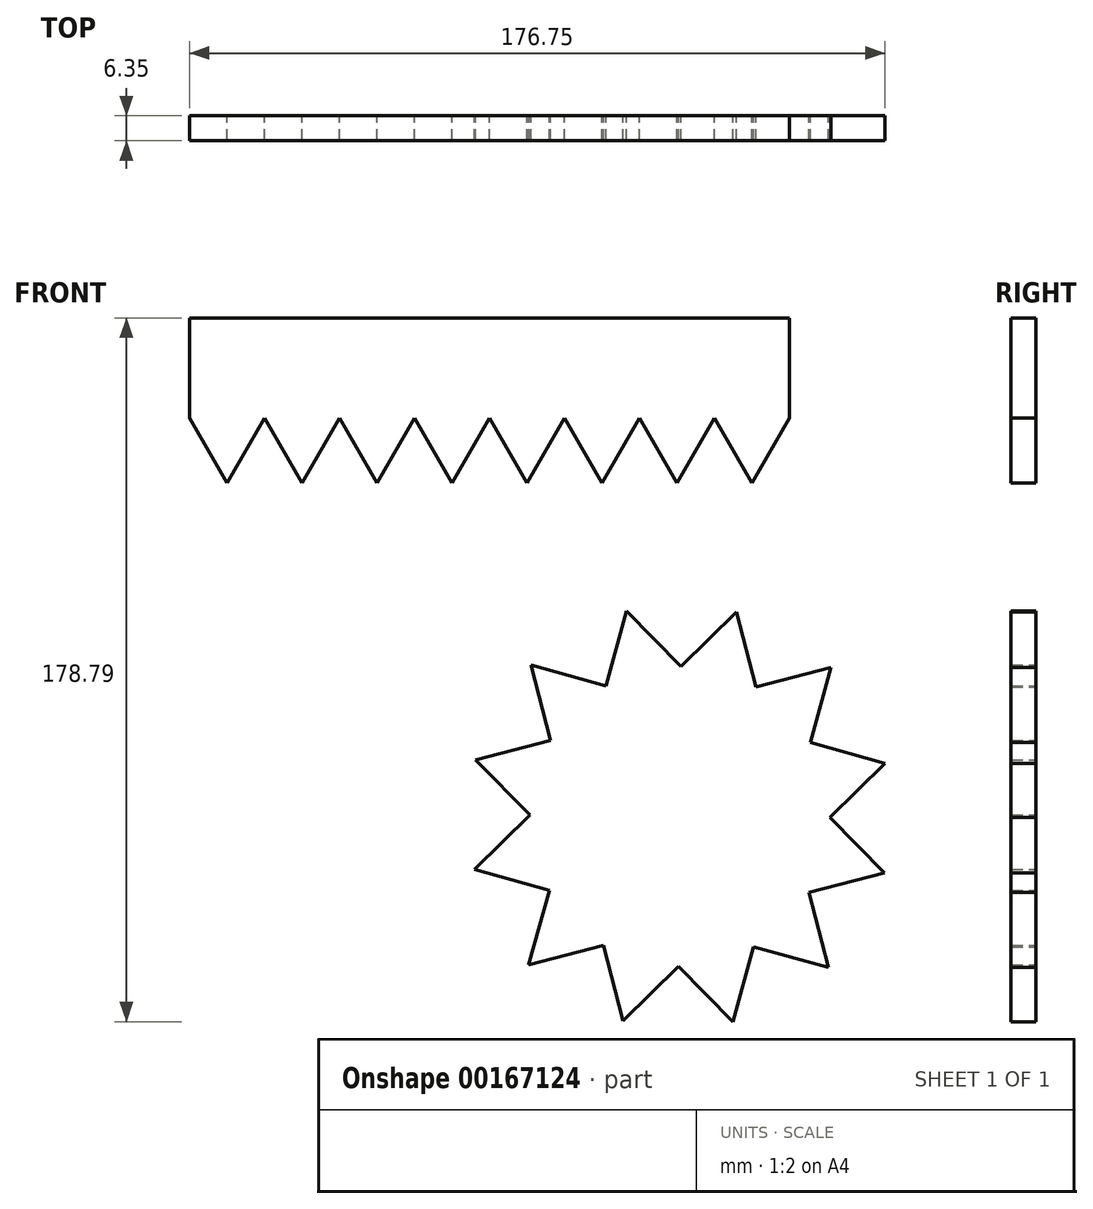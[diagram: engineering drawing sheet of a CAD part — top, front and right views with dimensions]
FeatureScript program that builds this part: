
annotation { "Feature Type Name" : "Feature", "Feature Type Description" : "" }
export const myFeature = defineFeature(function(context is Context, id is Id, definition is map)
    precondition{}
    {
        {
            var Q0;
            Q0=qCreatedBy(makeId("Front.planeOp"),FACE);
            var sketch = newSketch(context, id + "F0", { "sketchPlane" : qUnion([Q0])});
            skCircle(sketch, "E0", {"center": v(0, -57.84) * mm, "radius": 38.1 * mm});
            skCircle(sketch, "E1.cCircle", {"center": v(0, -57.84) * mm, "radius": 38.1 * mm, "construction": true});
            skLineSegment(sketch, "E1.0", {"start": v(33.16, -39.07) * mm, "end": v(38.1, -58.17) * mm});
            skLineSegment(sketch, "E1.1", {"start": v(38.1, -58.17) * mm, "end": v(32.83, -77.17) * mm});
            skLineSegment(sketch, "E1.2", {"start": v(32.83, -77.17) * mm, "end": v(18.77, -91) * mm});
            skLineSegment(sketch, "E1.3", {"start": v(18.77, -91) * mm, "end": v(-0.33, -95.94) * mm});
            skLineSegment(sketch, "E1.4", {"start": v(-0.33, -95.94) * mm, "end": v(-19.33, -90.67) * mm});
            skLineSegment(sketch, "E1.5", {"start": v(-19.33, -90.67) * mm, "end": v(-33.16, -76.6) * mm});
            skLineSegment(sketch, "E1.6", {"start": v(-33.16, -76.6) * mm, "end": v(-38.1, -57.51) * mm});
            skLineSegment(sketch, "E1.7", {"start": v(-38.1, -57.51) * mm, "end": v(-32.83, -38.5) * mm});
            skLineSegment(sketch, "E1.8", {"start": v(-32.83, -38.5) * mm, "end": v(-18.77, -24.68) * mm});
            skLineSegment(sketch, "E1.9", {"start": v(-18.77, -24.68) * mm, "end": v(0.33, -19.74) * mm});
            skLineSegment(sketch, "E1.10", {"start": v(0.33, -19.74) * mm, "end": v(19.33, -25) * mm});
            skLineSegment(sketch, "E1.11", {"start": v(19.33, -25) * mm, "end": v(33.16, -39.07) * mm});
            skLineSegment(sketch, "E2", {"start": v(-32.83, -38.5) * mm, "end": v(-37.77, -19.42) * mm});
            skLineSegment(sketch, "E3", {"start": v(-37.77, -19.42) * mm, "end": v(-18.77, -24.68) * mm});
            skLineSegment(sketch, "E4.1.0", {"start": v(-38.1, -57.51) * mm, "end": v(-51.92, -43.45) * mm});
            skLineSegment(sketch, "E4.1.1", {"start": v(-51.92, -43.45) * mm, "end": v(-32.83, -38.5) * mm});
            skLineSegment(sketch, "E4.2.0", {"start": v(-33.16, -76.6) * mm, "end": v(-52.16, -71.34) * mm});
            skLineSegment(sketch, "E4.2.1", {"start": v(-52.16, -71.34) * mm, "end": v(-38.1, -57.51) * mm});
            skLineSegment(sketch, "E4.3.0", {"start": v(-19.33, -90.67) * mm, "end": v(-38.43, -95.61) * mm});
            skLineSegment(sketch, "E4.3.1", {"start": v(-38.43, -95.61) * mm, "end": v(-33.16, -76.6) * mm});
            skLineSegment(sketch, "E4.4.0", {"start": v(-0.33, -95.94) * mm, "end": v(-14.4, -109.76) * mm});
            skLineSegment(sketch, "E4.4.1", {"start": v(-14.4, -109.76) * mm, "end": v(-19.33, -90.67) * mm});
            skLineSegment(sketch, "E4.5.0", {"start": v(18.77, -91) * mm, "end": v(13.5, -110) * mm});
            skLineSegment(sketch, "E4.5.1", {"start": v(13.5, -110) * mm, "end": v(-0.33, -95.94) * mm});
            skLineSegment(sketch, "E4.6.0", {"start": v(32.83, -77.17) * mm, "end": v(37.77, -96.27) * mm});
            skLineSegment(sketch, "E4.6.1", {"start": v(37.77, -96.27) * mm, "end": v(18.77, -91) * mm});
            skLineSegment(sketch, "E4.7.0", {"start": v(38.1, -58.17) * mm, "end": v(51.92, -72.23) * mm});
            skLineSegment(sketch, "E4.7.1", {"start": v(51.92, -72.23) * mm, "end": v(32.83, -77.17) * mm});
            skLineSegment(sketch, "E4.8.0", {"start": v(33.16, -39.07) * mm, "end": v(52.16, -44.34) * mm});
            skLineSegment(sketch, "E4.8.1", {"start": v(52.16, -44.34) * mm, "end": v(38.1, -58.17) * mm});
            skLineSegment(sketch, "E4.9.0", {"start": v(19.33, -25) * mm, "end": v(38.43, -20.07) * mm});
            skLineSegment(sketch, "E4.9.1", {"start": v(38.43, -20.07) * mm, "end": v(33.16, -39.07) * mm});
            skLineSegment(sketch, "E4.10.0", {"start": v(0.33, -19.74) * mm, "end": v(14.4, -5.92) * mm});
            skLineSegment(sketch, "E4.10.1", {"start": v(14.4, -5.92) * mm, "end": v(19.33, -25) * mm});
            skLineSegment(sketch, "E4.11.0", {"start": v(-18.77, -24.68) * mm, "end": v(-13.5, -5.68) * mm});
            skLineSegment(sketch, "E4.11.1", {"start": v(-13.5, -5.68) * mm, "end": v(0.33, -19.74) * mm});
            skSolve(sketch);
        }
        {
            var Q0;
            Q0 = qSketchRegion(id + "F0", true);
            extrude(context, id + "F1", {"entities" : qUnion([Q0]), "depth" : 6.35 * mm});
        }
        {
            var Q0;
            Q0=qCreatedBy(makeId("Front.planeOp"),FACE);
            var sketch = newSketch(context, id + "F2", { "sketchPlane" : qUnion([Q0])});
            skLineSegment(sketch, "E5.bottom", {"start": v(-124.6, 68.79) * mm, "end": v(27.8, 68.79) * mm});
            skLineSegment(sketch, "E5.top", {"start": v(-124.6, 43.39) * mm, "end": v(27.8, 43.39) * mm});
            skLineSegment(sketch, "E5.left", {"start": v(-124.6, 68.79) * mm, "end": v(-124.6, 43.39) * mm});
            skLineSegment(sketch, "E5.right", {"start": v(27.8, 68.79) * mm, "end": v(27.8, 43.39) * mm});
            skLineSegment(sketch, "E6", {"start": v(-124.6, 43.39) * mm, "end": v(-115.07, 26.89) * mm});
            skLineSegment(sketch, "E7", {"start": v(-115.07, 26.89) * mm, "end": v(-105.54, 43.39) * mm});
            skLineSegment(sketch, "E8.1.0.0", {"start": v(-105.54, 43.39) * mm, "end": v(-96.02, 26.89) * mm});
            skLineSegment(sketch, "E8.1.0.1", {"start": v(-105.54, 43.39) * mm, "end": v(46.86, 43.39) * mm});
            skLineSegment(sketch, "E8.1.0.2", {"start": v(-96.02, 26.89) * mm, "end": v(-86.5, 43.39) * mm});
            skLineSegment(sketch, "E8.2.0.0", {"start": v(-86.5, 43.39) * mm, "end": v(-76.97, 26.89) * mm});
            skLineSegment(sketch, "E8.2.0.1", {"start": v(-86.5, 43.39) * mm, "end": v(65.9, 43.39) * mm});
            skLineSegment(sketch, "E8.2.0.2", {"start": v(-76.97, 26.89) * mm, "end": v(-67.44, 43.39) * mm});
            skLineSegment(sketch, "E8.3.0.0", {"start": v(-67.44, 43.39) * mm, "end": v(-57.92, 26.89) * mm});
            skLineSegment(sketch, "E8.3.0.1", {"start": v(-67.44, 43.39) * mm, "end": v(84.96, 43.39) * mm});
            skLineSegment(sketch, "E8.3.0.2", {"start": v(-57.92, 26.89) * mm, "end": v(-48.4, 43.39) * mm});
            skLineSegment(sketch, "E8.4.0.0", {"start": v(-48.4, 43.39) * mm, "end": v(-38.87, 26.89) * mm});
            skLineSegment(sketch, "E8.4.0.1", {"start": v(-48.4, 43.39) * mm, "end": v(104, 43.39) * mm});
            skLineSegment(sketch, "E8.4.0.2", {"start": v(-38.87, 26.89) * mm, "end": v(-29.34, 43.39) * mm});
            skLineSegment(sketch, "E8.5.0.0", {"start": v(-29.34, 43.39) * mm, "end": v(-19.82, 26.89) * mm});
            skLineSegment(sketch, "E8.5.0.1", {"start": v(-29.34, 43.39) * mm, "end": v(123.06, 43.39) * mm});
            skLineSegment(sketch, "E8.5.0.2", {"start": v(-19.82, 26.89) * mm, "end": v(-10.3, 43.39) * mm});
            skLineSegment(sketch, "E8.6.0.0", {"start": v(-10.3, 43.39) * mm, "end": v(-0.77, 26.89) * mm});
            skLineSegment(sketch, "E8.6.0.1", {"start": v(-10.3, 43.39) * mm, "end": v(142.1, 43.39) * mm});
            skLineSegment(sketch, "E8.6.0.2", {"start": v(-0.77, 26.89) * mm, "end": v(8.76, 43.39) * mm});
            skLineSegment(sketch, "E8.7.0.0", {"start": v(8.76, 43.39) * mm, "end": v(18.28, 26.89) * mm});
            skLineSegment(sketch, "E8.7.0.1", {"start": v(8.76, 43.39) * mm, "end": v(161.16, 43.39) * mm});
            skLineSegment(sketch, "E8.7.0.2", {"start": v(18.28, 26.89) * mm, "end": v(27.8, 43.39) * mm});
            skLineSegment(sketch, "E8.direction1", {"start": v(-115.07, 26.89) * mm, "end": v(-96.02, 26.89) * mm, "construction": true});
            skSolve(sketch);
        }
        {
            var Q0;
            Q0 = qSketchRegion(id + "F2", true);
            extrude(context, id + "F3", {"entities" : qUnion([Q0]), "depth" : 6.35 * mm});
        }
    });
